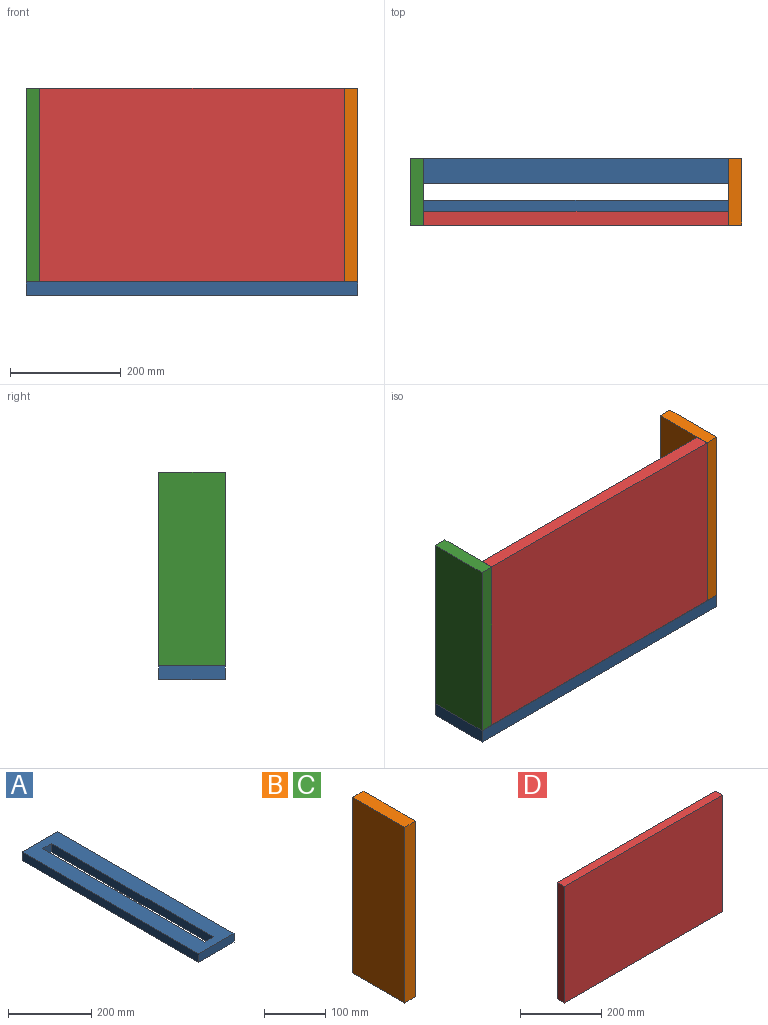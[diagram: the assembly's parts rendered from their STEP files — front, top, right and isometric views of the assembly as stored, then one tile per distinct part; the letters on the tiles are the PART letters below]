
ASSEMBLY  parts=4 mates=9
PART A: 10 faces, bbox 120x600x25 mm
  f0: plane 600x120mm, normal (0,0,1), area 55500mm2, adj f2,f3,f4,f5,f6,f7,f8,f9
  f1: plane 600x120mm, normal (0,0,-1), area 55500mm2, adj f2,f3,f4,f5,f6,f7,f8,f9
  f2: plane 120x25mm, normal (0,-1,0), area 3000mm2, adj f0,f1,f3,f5
  f3: plane 600x25mm, normal (1,0,0), area 15000mm2, adj f0,f1,f2,f4
  f4: plane 120x25mm, normal (0,1,0), area 3000mm2, adj f0,f1,f3,f5
  f5: plane 600x25mm, normal (-1,0,0), area 15000mm2, adj f0,f1,f2,f4
  f6: plane 30x25mm, normal (0,-1,0), area 750mm2, adj f0,f1,f7,f9
  f7: plane 550x25mm, normal (1,0,0), area 13750mm2, adj f0,f1,f6,f8
  f8: plane 30x25mm, normal (0,1,0), area 750mm2, adj f0,f1,f7,f9
  f9: plane 550x25mm, normal (-1,0,0), area 13750mm2, adj f0,f1,f6,f8
PART B: 6 faces, bbox 25x120x350 mm
  f0: plane 350x25mm, normal (0,-1,0), area 8750mm2, adj f1,f3,f4,f5
  f1: plane 120x25mm, normal (0,0,-1), area 3000mm2, adj f0,f2,f4,f5
  f2: plane 350x25mm, normal (0,1,0), area 8750mm2, adj f1,f3,f4,f5
  f3: plane 120x25mm, normal (0,0,1), area 3000mm2, adj f0,f2,f4,f5
  f4: plane 350x120mm, normal (1,0,0), area 42000mm2, adj f0,f1,f2,f3
  f5: plane 350x120mm, normal (-1,0,0), area 42000mm2, adj f0,f1,f2,f3
PART C: same geometry as B
PART D: 6 faces, bbox 550x25x350 mm
  f0: plane 350x25mm, normal (-1,0,0), area 8750mm2, adj f1,f3,f4,f5
  f1: plane 550x25mm, normal (0,0,-1), area 13750mm2, adj f0,f2,f4,f5
  f2: plane 350x25mm, normal (1,0,0), area 8750mm2, adj f1,f3,f4,f5
  f3: plane 550x25mm, normal (0,0,1), area 13750mm2, adj f0,f2,f4,f5
  f4: plane 550x350mm, normal (0,-1,0), area 192500mm2, adj f0,f1,f2,f3
  f5: plane 550x350mm, normal (0,1,0), area 192500mm2, adj f0,f1,f2,f3
PLACE A rot(axis=(0,0,-1),90deg) t=(-51.08,201.04,-268.8)mm
PLACE B t=(223.92,201.04,-68.8)mm
PLACE C t=(-351.08,201.04,-68.8)mm
PLACE D t=(-51.08,166.04,-68.8)mm fixed
MATE planar D.f2 <-> B.f5  axis (1,0,0) through (223.92,153.54,-68.8)mm
MATE planar A.f5 <-> B.f2  axis (0,1,0) through (248.92,261.04,-243.8)mm
MATE planar B.f3 <-> D.f3  axis (0,0,1) through (236.42,201.04,106.2)mm
MATE planar C.f4 <-> D.f0  axis (1,0,0) through (-326.08,201.04,-68.8)mm
MATE planar C.f0 <-> D.f4  axis (0,-1,0) through (-338.58,141.04,-68.8)mm
MATE planar B.f0 <-> D.f4  axis (0,-1,0) through (236.42,141.04,-68.8)mm
MATE planar C.f3 <-> D.f3  axis (0,0,1) through (-338.58,201.04,106.2)mm
MATE planar A.f4 <-> B.f4  axis (1,0,0) through (248.92,201.04,-256.3)mm
MATE planar A.f0 <-> D.f1  axis (0,0,1) through (-51.08,201.04,-243.8)mm
